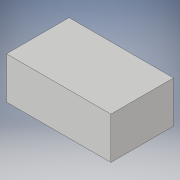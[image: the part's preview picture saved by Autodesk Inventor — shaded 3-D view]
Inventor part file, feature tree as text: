
AUTODESK INVENTOR PART (.ipt)
format: ipt  version: 2019.3 (Build 233278000, 278)  size: 86,016 bytes
history: native  units: mm
features: extrude x1, sketch x1
ambient origin geometry x8: Origin, YZ Plane, XZ Plane, XY Plane, X Axis, Y Axis, Z Axis, Center Point
bodies: Solid1 (feature_tree)
feature tree (2):
  extrude  "Extrusion1"  Depth=60.0mm
  sketch  "Sketch1"  dims[d0=36.0mm d1=60.0mm d2=24.0mm d3=0.0mm]
